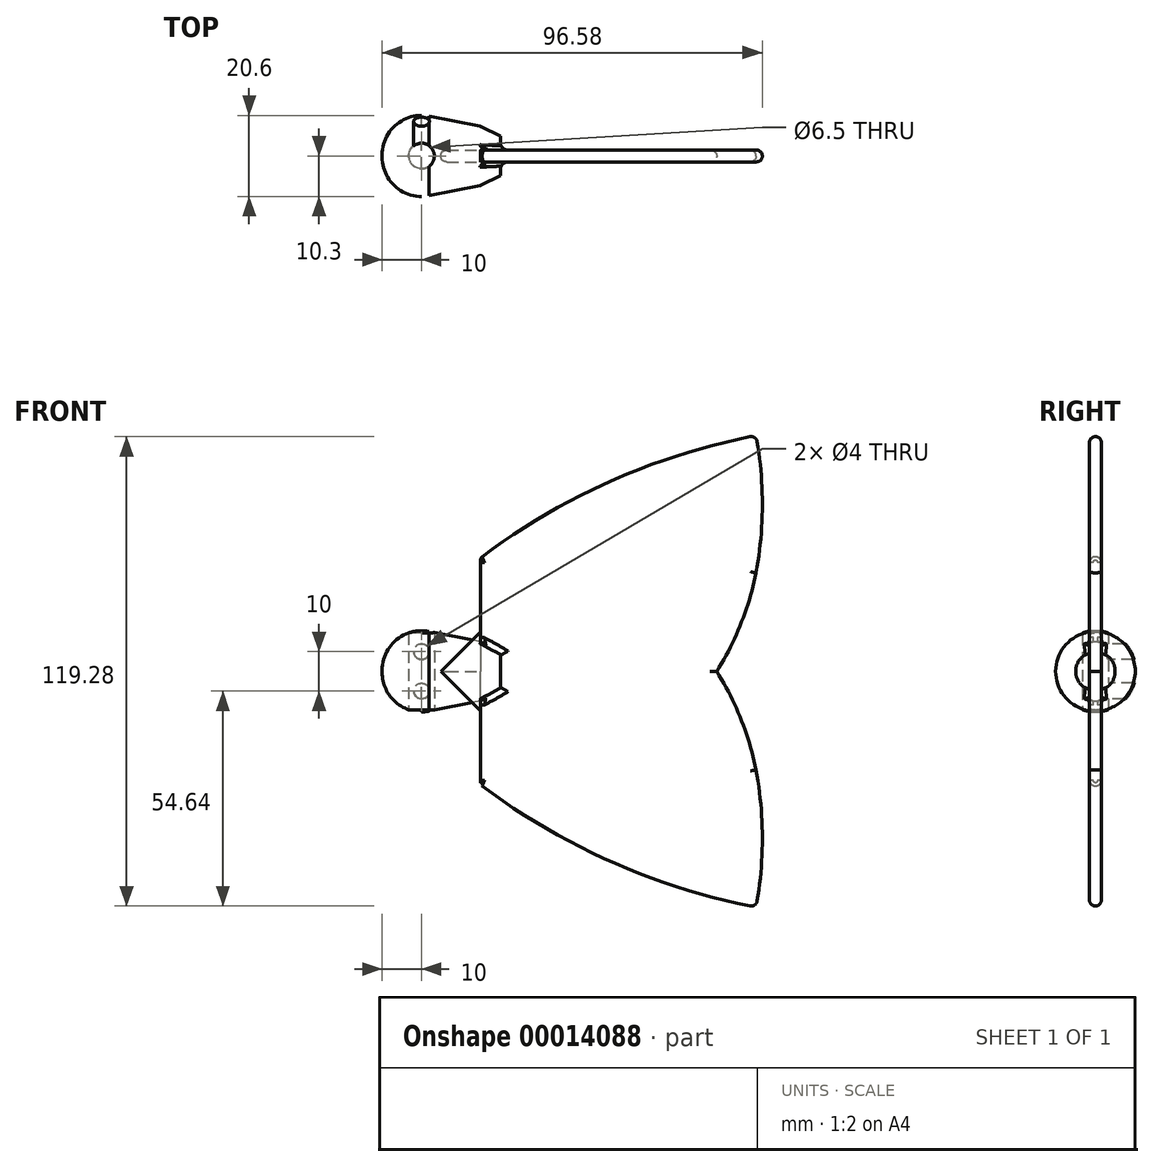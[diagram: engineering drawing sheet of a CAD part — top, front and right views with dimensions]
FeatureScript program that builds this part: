
annotation { "Feature Type Name" : "Feature", "Feature Type Description" : "" }
export const myFeature = defineFeature(function(context is Context, id is Id, definition is map)
    precondition{}
    {
        {
            var Q0;
            Q0=qCreatedBy(makeId("Front.planeOp"),FACE);
            var sketch = newSketch(context, id + "F0", { "sketchPlane" : qUnion([Q0])});
            skArc(sketch, "E0", {"start": v(70, 59.9) * mm, "mid": v(33.22, 48.38) * mm, "end": v(0, 28.82) * mm});
            skArc(sketch, "E1", {"start": v(70, 25.02) * mm, "mid": v(71.58, 42.46) * mm, "end": v(70, 59.9) * mm});
            skArc(sketch, "E2", {"start": v(60, 0) * mm, "mid": v(66.12, 12.07) * mm, "end": v(70, 25.02) * mm});
            skLineSegment(sketch, "E3", {"start": v(0, 28.82) * mm, "end": v(0, 0) * mm});
            skLineSegment(sketch, "E4", {"start": v(0, 0) * mm, "end": v(60, 0) * mm});
            skLineSegment(sketch, "E5", {"start": v(0, 10) * mm, "end": v(-10, 0) * mm});
            skLineSegment(sketch, "E6", {"start": v(-10, 0) * mm, "end": v(0, 0) * mm});
            skSolve(sketch);
        }
        {
            var Q0;
            Q0=makeQuery(id+"F0.imprint","IMPRINT",FACE,{"disambiguationData":[TD([[makeQuery(id+"F0.imprint","IMPRINT",EDGE,{"derivedFrom":sQuery(id+"F0.wireOp",EDGE,"E0")}),1.0]])]});
            extrude(context, id + "F1", {"entities" : qUnion([Q0]), "endBound" : BoundingType.SYMMETRIC, "depth" : 3 * mm});
        }
        {
            var Q0;
            Q0=makeQuery(id+"F1.opExtrude","CAP_EDGE",EDGE,{"disambiguationData":[OSD([sQuery(id+"F0.wireOp",EDGE,"E0")])],"isStart":false});
            var Q1;
            Q1=makeQuery(id+"F1.opExtrude","CAP_EDGE",EDGE,{"disambiguationData":[OSD([sQuery(id+"F0.wireOp",EDGE,"E0")])],"isStart":true});
            fillet(context, id + "F2", {"entities" : qUnion([Q0, Q1]), "radius" : 1.5 * mm, "tangentPropagation" : true, "allowEdgeOverflow" : false});
        }
        {
            var Q0;
            Q0=makeQuery(id+"F1.opExtrude","CAP_EDGE",EDGE,{"disambiguationData":[OSD([sQuery(id+"F0.wireOp",EDGE,"E1")])],"isStart":false});
            var Q1;
            Q1=makeQuery(id+"F1.opExtrude","CAP_EDGE",EDGE,{"disambiguationData":[OSD([sQuery(id+"F0.wireOp",EDGE,"E2")])],"isStart":false});
            var Q2;
            Q2=makeQuery(id+"F1.opExtrude","CAP_EDGE",EDGE,{"disambiguationData":[OSD([sQuery(id+"F0.wireOp",EDGE,"E1")])],"isStart":true});
            var Q3;
            Q3=makeQuery(id+"F1.opExtrude","CAP_EDGE",EDGE,{"disambiguationData":[OSD([sQuery(id+"F0.wireOp",EDGE,"E2")])],"isStart":true});
            fillet(context, id + "F3", {"entities" : qUnion([Q0, Q1, Q2, Q3]), "radius" : 1.5 * mm, "tangentPropagation" : true, "allowEdgeOverflow" : false});
        }
        {
            var Q0;
            Q0=makeQuery(id+"F1.opExtrude","SWEPT_BODY",BODY,{"disambiguationData":[OSD([sQuery(id+"F0.wireOp",EDGE,"E0"),sQuery(id+"F0.wireOp",EDGE,"E1"),sQuery(id+"F0.wireOp",EDGE,"E2"),sQuery(id+"F0.wireOp",EDGE,"E3"),sQuery(id+"F0.wireOp",EDGE,"E4")])]});
            var Q1;
            Q1=qCreatedBy(makeId("Top.planeOp"),FACE);
            mirror(context, id + "F4", {"operationType" : NewBodyOperationType.ADD, "entities" : qUnion([Q0]), "mirrorPlane" : qUnion([Q1])});
        }
        {
            var Q0;
            Q0=qCreatedBy(makeId("Right.planeOp"),FACE);
            var sketch = newSketch(context, id + "F5", { "sketchPlane" : qUnion([Q0])});
            skCircle(sketch, "E7", {"center": v(0, 0) * mm, "radius": 7.5 * mm});
            skSolve(sketch);
        }
        {
            var Q0;
            Q0=qCreatedBy(makeId("Right.planeOp"),FACE);
            cPlane(context, id + "F6", {"entities" : qUnion([Q0]), "cplaneType" : CPlaneType.OFFSET, "offset" : 25 * mm, "oppositeDirection" : true, "width" : 150 * mm, "height" : 150 * mm});
        }
        {
            var Q0;
            Q0=qCreatedBy(id+"F6.planeOp",FACE);
            var sketch = newSketch(context, id + "F7", { "sketchPlane" : qUnion([Q0])});
            skCircle(sketch, "E8", {"center": v(0, 0) * mm, "radius": 12.5 * mm});
            skSolve(sketch);
        }
        {
            var Q0;
            Q0=makeQuery(id+"F5.imprint","IMPRINT",FACE,{"disambiguationData":[TD([[makeQuery(id+"F5.imprint","IMPRINT",EDGE,{"derivedFrom":sQuery(id+"F5.wireOp",EDGE,"E7")}),1.0]])]});
            var Q1;
            Q1=makeQuery(id+"F7.imprint","IMPRINT",FACE,{"disambiguationData":[TD([[makeQuery(id+"F7.imprint","IMPRINT",EDGE,{"derivedFrom":sQuery(id+"F7.wireOp",EDGE,"E8")}),1.0]])]});
            loft(context, id + "F8", {"sheetProfilesArray" : [{ "sheetProfileEntities" : qUnion([Q0]) }, { "sheetProfileEntities" : qUnion([Q1]) }]});
        }
        {
            var Q0;
            Q0=qCreatedBy(makeId("Right.planeOp"),FACE);
            cPlane(context, id + "F9", {"entities" : qUnion([Q0]), "cplaneType" : CPlaneType.OFFSET, "offset" : 5 * mm, "width" : 150 * mm, "height" : 150 * mm});
        }
        {
            var Q0;
            Q0=qCreatedBy(id+"F9.planeOp",FACE);
            var sketch = newSketch(context, id + "F10", { "sketchPlane" : qUnion([Q0])});
            skCircle(sketch, "E9", {"center": v(0, 0) * mm, "radius": 5 * mm});
            skSolve(sketch);
        }
        {
            var Q0;
            Q0 = qSketchRegion(id + "F5", true);
            var Q1;
            Q1 = qSketchRegion(id + "F10", true);
            loft(context, id + "F11", {"operationType" : NewBodyOperationType.ADD, "sheetProfilesArray" : [{ "sheetProfileEntities" : qUnion([Q0]) }, { "sheetProfileEntities" : qUnion([Q1]) }]});
        }
        {
            var Q0;
            {var subQ0=makeQuery(id+"F1.opExtrude","CAP_FACE",FACE,{"disambiguationData":[OSD([sQuery(id+"F0.wireOp",EDGE,"E0"),sQuery(id+"F0.wireOp",EDGE,"E1"),sQuery(id+"F0.wireOp",EDGE,"E2"),sQuery(id+"F0.wireOp",EDGE,"E3"),sQuery(id+"F0.wireOp",EDGE,"E4")])],"isStart":false});Q0=makeQuery(id+"F11.boolean.opBoolean","INTERSECT",EDGE,{"derivedFrom":[makeQuery(id+"F4.boolean.opBoolean","MERGE",FACE,{"derivedFrom":[subQ0,makeQuery(id+"F4.opPattern","COPY",FACE,{"derivedFrom":subQ0,"instanceName":"1"})]}),makeQuery(id+"F11.opLoft","CAP_FACE",FACE,{"disambiguationData":[OSD([makeQuery(id+"F10.imprint","IMPRINT",FACE,{"disambiguationData":[TD([[makeQuery(id+"F10.imprint","IMPRINT",EDGE,{"derivedFrom":sQuery(id+"F10.wireOp",EDGE,"E9")}),1.0]])]})])],"isStart":true})]});}
            var Q1;
            {var subQ0=makeQuery(id+"F1.opExtrude","CAP_FACE",FACE,{"disambiguationData":[OSD([sQuery(id+"F0.wireOp",EDGE,"E0"),sQuery(id+"F0.wireOp",EDGE,"E1"),sQuery(id+"F0.wireOp",EDGE,"E2"),sQuery(id+"F0.wireOp",EDGE,"E3"),sQuery(id+"F0.wireOp",EDGE,"E4")])],"isStart":false});Q1=makeQuery(id+"F11.boolean.opBoolean","INTERSECT",EDGE,{"disambiguationData":[OD(0.0)],"derivedFrom":[makeQuery(id+"F4.boolean.opBoolean","MERGE",FACE,{"derivedFrom":[subQ0,makeQuery(id+"F4.opPattern","COPY",FACE,{"derivedFrom":subQ0,"instanceName":"1"})]}),makeQuery(id+"F11.opLoft","SWEPT_FACE",FACE,{"disambiguationData":[OSD([sQuery(id+"F5.wireOp",EDGE,"E7"),sQuery(id+"F10.wireOp",EDGE,"E9")])]})]});}
            var Q2;
            {var subQ0=makeQuery(id+"F1.opExtrude","CAP_FACE",FACE,{"disambiguationData":[OSD([sQuery(id+"F0.wireOp",EDGE,"E0"),sQuery(id+"F0.wireOp",EDGE,"E1"),sQuery(id+"F0.wireOp",EDGE,"E2"),sQuery(id+"F0.wireOp",EDGE,"E3"),sQuery(id+"F0.wireOp",EDGE,"E4")])],"isStart":false});Q2=makeQuery(id+"F11.boolean.opBoolean","INTERSECT",EDGE,{"disambiguationData":[OD(1.0)],"derivedFrom":[makeQuery(id+"F4.boolean.opBoolean","MERGE",FACE,{"derivedFrom":[subQ0,makeQuery(id+"F4.opPattern","COPY",FACE,{"derivedFrom":subQ0,"instanceName":"1"})]}),makeQuery(id+"F11.opLoft","SWEPT_FACE",FACE,{"disambiguationData":[OSD([sQuery(id+"F5.wireOp",EDGE,"E7"),sQuery(id+"F10.wireOp",EDGE,"E9")])]})]});}
            var Q3;
            {var subQ0=makeQuery(id+"F1.opExtrude","CAP_FACE",FACE,{"disambiguationData":[OSD([sQuery(id+"F0.wireOp",EDGE,"E0"),sQuery(id+"F0.wireOp",EDGE,"E1"),sQuery(id+"F0.wireOp",EDGE,"E2"),sQuery(id+"F0.wireOp",EDGE,"E3"),sQuery(id+"F0.wireOp",EDGE,"E4")])],"isStart":true});Q3=makeQuery(id+"F11.boolean.opBoolean","INTERSECT",EDGE,{"disambiguationData":[OD(0.0)],"derivedFrom":[makeQuery(id+"F4.boolean.opBoolean","MERGE",FACE,{"derivedFrom":[subQ0,makeQuery(id+"F4.opPattern","COPY",FACE,{"derivedFrom":subQ0,"instanceName":"1"})]}),makeQuery(id+"F11.opLoft","SWEPT_FACE",FACE,{"disambiguationData":[OSD([sQuery(id+"F5.wireOp",EDGE,"E7"),sQuery(id+"F10.wireOp",EDGE,"E9")])]})]});}
            var Q4;
            {var subQ0=makeQuery(id+"F1.opExtrude","CAP_FACE",FACE,{"disambiguationData":[OSD([sQuery(id+"F0.wireOp",EDGE,"E0"),sQuery(id+"F0.wireOp",EDGE,"E1"),sQuery(id+"F0.wireOp",EDGE,"E2"),sQuery(id+"F0.wireOp",EDGE,"E3"),sQuery(id+"F0.wireOp",EDGE,"E4")])],"isStart":true});Q4=makeQuery(id+"F11.boolean.opBoolean","INTERSECT",EDGE,{"derivedFrom":[makeQuery(id+"F4.boolean.opBoolean","MERGE",FACE,{"derivedFrom":[subQ0,makeQuery(id+"F4.opPattern","COPY",FACE,{"derivedFrom":subQ0,"instanceName":"1"})]}),makeQuery(id+"F11.opLoft","CAP_FACE",FACE,{"disambiguationData":[OSD([makeQuery(id+"F10.imprint","IMPRINT",FACE,{"disambiguationData":[TD([[makeQuery(id+"F10.imprint","IMPRINT",EDGE,{"derivedFrom":sQuery(id+"F10.wireOp",EDGE,"E9")}),1.0]])]})])],"isStart":true})]});}
            var Q5;
            {var subQ0=makeQuery(id+"F1.opExtrude","CAP_FACE",FACE,{"disambiguationData":[OSD([sQuery(id+"F0.wireOp",EDGE,"E0"),sQuery(id+"F0.wireOp",EDGE,"E1"),sQuery(id+"F0.wireOp",EDGE,"E2"),sQuery(id+"F0.wireOp",EDGE,"E3"),sQuery(id+"F0.wireOp",EDGE,"E4")])],"isStart":true});Q5=makeQuery(id+"F11.boolean.opBoolean","INTERSECT",EDGE,{"disambiguationData":[OD(1.0)],"derivedFrom":[makeQuery(id+"F4.boolean.opBoolean","MERGE",FACE,{"derivedFrom":[subQ0,makeQuery(id+"F4.opPattern","COPY",FACE,{"derivedFrom":subQ0,"instanceName":"1"})]}),makeQuery(id+"F11.opLoft","SWEPT_FACE",FACE,{"disambiguationData":[OSD([sQuery(id+"F5.wireOp",EDGE,"E7"),sQuery(id+"F10.wireOp",EDGE,"E9")])]})]});}
            fillet(context, id + "F12", {"entities" : qUnion([Q0, Q1, Q2, Q3, Q4, Q5]), "radius" : 2 * mm, "tangentPropagation" : true, "allowEdgeOverflow" : false});
        }
        {
            var Q0;
            Q0=makeQuery(id+"F8.opLoft","MID_CAP_EDGE",EDGE,{"disambiguationData":[OSD([sQuery(id+"F5.wireOp",EDGE,"E7"),sQuery(id+"F7.wireOp",EDGE,"E8")])],"capPos":1.0});
            fillet(context, id + "F13", {"entities" : qUnion([Q0]), "radius" : 10 * mm, "tangentPropagation" : true, "allowEdgeOverflow" : false});
        }
        {
            var Q0;
            Q0=qCreatedBy(makeId("Top.planeOp"),FACE);
            var sketch = newSketch(context, id + "F14", { "sketchPlane" : qUnion([Q0])});
            skCircle(sketch, "E10", {"center": v(-15, 0) * mm, "radius": 3.25 * mm});
            skSolve(sketch);
        }
        {
            var Q0;
            Q0 = qSketchRegion(id + "F14", true);
            extrude(context, id + "F15", {"entities" : qUnion([Q0]), "operationType" : NewBodyOperationType.REMOVE, "endBound" : BoundingType.THROUGH_ALL, "depth" : 25 * mm, "hasSecondDirection" : true, "secondDirectionOppositeDirection" : true, "secondDirectionDepth" : 25 * mm});
        }
        {
            var Q0;
            Q0=qCreatedBy(makeId("Front.planeOp"),FACE);
            var sketch = newSketch(context, id + "F16", { "sketchPlane" : qUnion([Q0])});
            skCircle(sketch, "E11", {"center": v(-15, 5) * mm, "radius": 2 * mm});
            skCircle(sketch, "E12", {"center": v(-15, -5) * mm, "radius": 2 * mm});
            skSolve(sketch);
        }
        {
            var Q0;
            Q0 = qSketchRegion(id + "F16", true);
            extrude(context, id + "F17", {"entities" : qUnion([Q0]), "operationType" : NewBodyOperationType.REMOVE, "endBound" : BoundingType.THROUGH_ALL, "oppositeDirection" : true, "depth" : 25 * mm});
        }
        {
            var Q0;
            {var subQ1=sQuery(id+"F0.wireOp",EDGE,"E5");Q0=makeQuery(id+"F0.imprint","IMPRINT",FACE,{"disambiguationData":[TD([[makeQuery(id+"F0.imprint","IMPRINT",EDGE,{"derivedFrom":subQ1}),1.0]])]});}
            extrude(context, id + "F18", {"entities" : qUnion([Q0]), "endBound" : BoundingType.SYMMETRIC, "depth" : 3 * mm});
        }
        {
            var Q0;
            Q0=makeQuery(id+"F18.opExtrude","SWEPT_BODY",BODY,{"disambiguationData":[OSD([sQuery(id+"F0.wireOp",EDGE,"E3"),sQuery(id+"F0.wireOp",EDGE,"E5"),sQuery(id+"F0.wireOp",EDGE,"E6")])]});
            var Q1;
            Q1=qCreatedBy(makeId("Top.planeOp"),FACE);
            mirror(context, id + "F19", {"entities" : qUnion([Q0]), "mirrorPlane" : qUnion([Q1])});
        }
        {
            var Q0;
            Q0=makeQuery(id+"F18.opExtrude","CAP_EDGE",EDGE,{"disambiguationData":[OSD([sQuery(id+"F0.wireOp",EDGE,"E5")])],"isStart":false});
            var Q1;
            Q1=makeQuery(id+"F18.opExtrude","CAP_EDGE",EDGE,{"disambiguationData":[OSD([sQuery(id+"F0.wireOp",EDGE,"E5")])],"isStart":true});
            var Q2;
            Q2=makeQuery(id+"F19.opPattern","COPY",EDGE,{"derivedFrom":makeQuery(id+"F18.opExtrude","CAP_EDGE",EDGE,{"disambiguationData":[OSD([sQuery(id+"F0.wireOp",EDGE,"E5")])],"isStart":false}),"instanceName":"1"});
            var Q3;
            Q3=makeQuery(id+"F19.opPattern","COPY",EDGE,{"derivedFrom":makeQuery(id+"F18.opExtrude","CAP_EDGE",EDGE,{"disambiguationData":[OSD([sQuery(id+"F0.wireOp",EDGE,"E5")])],"isStart":true}),"instanceName":"1"});
            var Q4;
            {var subQ0=sQuery(id+"F0.wireOp",EDGE,"E3");var subQ1=makeQuery(id+"F1.opExtrude","CAP_EDGE",EDGE,{"disambiguationData":[OSD([subQ0])],"isStart":true});var subQ4=sQuery(id+"F0.wireOp",EDGE,"E0");Q4=makeQuery(id+"F11.boolean.opBoolean","SPLIT",EDGE,{"disambiguationData":[TD([makeQuery(id+"F2.opFillet","BLEND_FACE",FACE,{"disambiguationData":[OSD([subQ4])]})])],"derivedFrom":makeQuery(id+"F4.boolean.opBoolean","MERGE",EDGE,{"derivedFrom":[subQ1,makeQuery(id+"F4.opPattern","COPY",EDGE,{"derivedFrom":subQ1,"instanceName":"1"})]})});}
            var Q5;
            {var subQ0=sQuery(id+"F0.wireOp",EDGE,"E3");var subQ1=makeQuery(id+"F1.opExtrude","CAP_EDGE",EDGE,{"disambiguationData":[OSD([subQ0])],"isStart":false});var subQ3=sQuery(id+"F0.wireOp",EDGE,"E0");Q5=makeQuery(id+"F11.boolean.opBoolean","SPLIT",EDGE,{"disambiguationData":[TD([makeQuery(id+"F2.opFillet","BLEND_FACE",FACE,{"disambiguationData":[OSD([subQ3])]})])],"derivedFrom":makeQuery(id+"F4.boolean.opBoolean","MERGE",EDGE,{"derivedFrom":[subQ1,makeQuery(id+"F4.opPattern","COPY",EDGE,{"derivedFrom":subQ1,"instanceName":"1"})]})});}
            var Q6;
            {var subQ0=sQuery(id+"F0.wireOp",EDGE,"E3");var subQ1=makeQuery(id+"F1.opExtrude","CAP_EDGE",EDGE,{"disambiguationData":[OSD([subQ0])],"isStart":true});var subQ3=sQuery(id+"F0.wireOp",EDGE,"E0");Q6=makeQuery(id+"F11.boolean.opBoolean","SPLIT",EDGE,{"disambiguationData":[TD([makeQuery(id+"F4.opPattern","COPY",FACE,{"derivedFrom":makeQuery(id+"F2.opFillet","BLEND_FACE",FACE,{"disambiguationData":[OSD([subQ3])]}),"instanceName":"1"})])],"derivedFrom":makeQuery(id+"F4.boolean.opBoolean","MERGE",EDGE,{"derivedFrom":[subQ1,makeQuery(id+"F4.opPattern","COPY",EDGE,{"derivedFrom":subQ1,"instanceName":"1"})]})});}
            var Q7;
            {var subQ0=sQuery(id+"F0.wireOp",EDGE,"E3");var subQ1=makeQuery(id+"F1.opExtrude","CAP_EDGE",EDGE,{"disambiguationData":[OSD([subQ0])],"isStart":false});var subQ3=sQuery(id+"F0.wireOp",EDGE,"E0");Q7=makeQuery(id+"F11.boolean.opBoolean","SPLIT",EDGE,{"disambiguationData":[TD([makeQuery(id+"F4.opPattern","COPY",FACE,{"derivedFrom":makeQuery(id+"F2.opFillet","BLEND_FACE",FACE,{"disambiguationData":[OSD([subQ3])]}),"instanceName":"1"})])],"derivedFrom":makeQuery(id+"F4.boolean.opBoolean","MERGE",EDGE,{"derivedFrom":[subQ1,makeQuery(id+"F4.opPattern","COPY",EDGE,{"derivedFrom":subQ1,"instanceName":"1"})]})});}
            fillet(context, id + "F20", {"entities" : qUnion([Q0, Q1, Q2, Q3, Q4, Q5, Q6, Q7]), "radius" : 1 * mm, "tangentPropagation" : true, "allowEdgeOverflow" : false});
        }
    });
